# Revit family: Stair_Tread-Wooster-Supergrit_Safety_Treads-610
name_source: partatom
category: Specialty Equipment
revit_build: Autodesk Revit 2017 (Build: 20160720_1515(x64)
units: mm (PartAtom-declared; Revit-internal decimal feet)

## family parameters
Cut with Voids When Loaded = No
Host = Face
OmniClass Number = 23.30.70.21.11.11.11
OmniClass Title = Stair Nosings
Part Type = Normal
Room Calculation Point = No
Round Connector Dimension = Use Diameter
Shared = No

## types (1)
- 610
    Construction Type = Existing Construction
    Default Elevation = 0' - 0"
    Depth = 0' - 0 1/4"
    Description = Anti-Slip Stair Nosing
    Manufacturer = Wooster Productions Inc
    Manufacturer Fax Number = 330-262-4151
    Model = 610
    Product Documentation Link = http://www.woosterproducts.com
    Product Name = Supergrit Nosings / Warning Strips
    Product Page URL = http://www.woosterproducts.com
    URL = http://www.wooster-products.com
    Version = 2017 - v2.0a

## geometry (parser evidence)
native form markers: Blend x19, Sweep x4
no freeform markers — native parametric forms only
